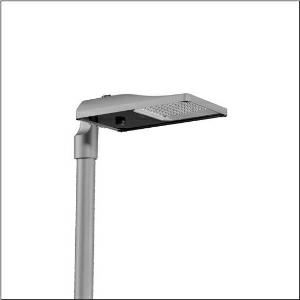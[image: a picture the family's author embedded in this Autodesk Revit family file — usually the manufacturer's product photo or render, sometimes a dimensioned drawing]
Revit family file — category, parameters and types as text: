
# Revit family: streetlight_sl_31_midi___st0_5a_5xh7b31t08ma_78a8
name_source: partatom
category: Lighting Fixtures
units: mm (PartAtom-declared; Revit-internal decimal feet)

## family parameters
Cut with Voids When Loaded = No
Host = Face
Light Source = No
Part Type = Normal
Room Calculation Point = No
Round Connector Dimension = Use Diameter
Shared = No

## types (1)
- --- (1 x LED, 19310 lm, 142.8 W, 3000K)
    Apparent Load = 143 VA
    CIE Flux Codes = 41 75 97 100 100
    Color Rendering = 70
    Color Temperature = 3000K
    Default Elevation = 1800 mm
    Description = Streetlight SL 31 midi D4i, Desk-Remote mast luminaire for post-top, side-entry; light control with lens of PMMA; light distribution: ST0.5a, direct asymmetric distribution, for standard-compliant lighting for roads and squares; LED: luminous flux: 19.310lm, light colour: 730, colour temperature: 3000K; luminous efficacy: 135,2lm/W; control: pre-setting: logarithmic dimming characteristic, flexible luminous flux parameterisation, time-dependent luminous flux control, constant luminous flux control, power reduction, intelligent temperature release in ECG and LED module, overheat protection; luminaire housing, of diecast aluminium, SITECO metallic grey (DB 702S), corrosivity category C5 high according to DIN EN ISO 12944; cover of toughened safety glass, transparent, opened without tools; mast flange of diecast aluminium, SITECO metallic grey (DB 702S), spigot size: 76/60mm, mast flange included unmounted; cable length: 12,5m, connection cable pre-assembled; mains connection: 220..240V, AC, 50/60Hz; power consumption (at start of service life): 142,8W / (at end of service life): 158,8W / (with reduced operation 50%): 60W; protection rating (complete): IP66; insulation class (complete): insulation class II (safety insulation); impact resistance: IK09; certification: CE, ENEC, ENEC+, VDE, UKCA, ZD4i; permissible operating ambient temperature for outdoor applications: -40..+50°C; packaging unit: 1 piece

Light Distribution: ST0.5a
    Height = 79 mm
    Lamp = 1 x LED
    Lamp Light Flux = 19310 lm
    Lamp Power = 142.8 W
    Lamp count = 1
    Length = 577 mm
    Luminous efficacy = 135 lm/W
    Manufacturer = Siteco
    ModVariant = No
    Model = 5XH7B31T08MA
    Number of Poles = 1
    OnlyDefault = Yes
    Power Factor = 1
    Product Name = Streetlight SL 31 midi | ST0.5a
    Product group = mast luminaire | pylon top
    ProductGroupID = 6100
    Protection Class = Protection class II
    Protection Degree = IP 66
    RLX_Detail_Level = 1
    RLX_Emergency_Light_Flux = 0 lm
    RLX_Emergency_Type = 0
    RLX_Emergency_Type_DB = No
    RlxData = <blob elided: 54125 chars, md5=82bf16f4>
    Socket = socket
    Standby Power = 0 W
    System Light Flux = 19309 lm
    System Power = 143 W
    Type Comments = factory setting: luminous flux: 100 % | dim-lin: 254 | 735 mA
    Type Image = l_1300321.jpg
    URL = http://relux.com
    VarID = @adj_064389
    Voltage = 0 V
    Weight = 0.00 kg
    Width = 362 mm

## geometry (parser evidence)
native form markers: Blend x4, Sweep x9
no freeform markers — native parametric forms only
